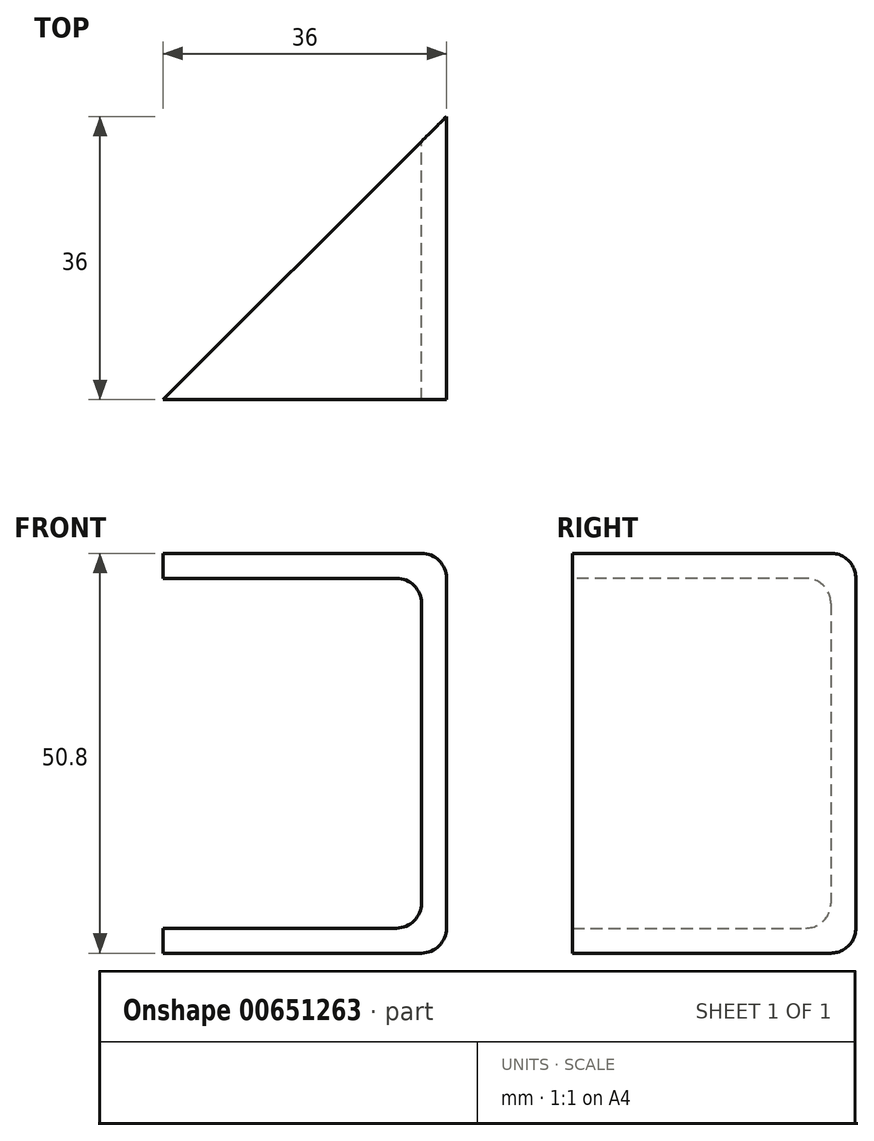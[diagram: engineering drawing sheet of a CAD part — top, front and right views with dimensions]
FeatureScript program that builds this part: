
annotation { "Feature Type Name" : "Feature", "Feature Type Description" : "" }
export const myFeature = defineFeature(function(context is Context, id is Id, definition is map)
    precondition{}
    {
        {
            var Q0;
            Q0=qCreatedBy(makeId("Front.planeOp"),FACE);
            var sketch = newSketch(context, id + "F0", { "sketchPlane" : qUnion([Q0])});
            skLineSegment(sketch, "E0.bottom", {"start": v(-38.1, -22.23) * mm, "end": v(-38.1, 22.22) * mm});
            skLineSegment(sketch, "E0.top", {"start": v(38.1, -22.23) * mm, "end": v(38.1, 22.22) * mm});
            skLineSegment(sketch, "E0.left", {"start": v(-34.92, -25.4) * mm, "end": v(34.93, -25.4) * mm});
            skLineSegment(sketch, "E0.right", {"start": v(-34.93, 25.4) * mm, "end": v(34.92, 25.4) * mm});
            skPoint(sketch, "E0.middle", {"position": v(0, 0) * mm});
            skLineSegment(sketch, "E1.bottom", {"start": v(34.93, 19.05) * mm, "end": v(34.93, -19.05) * mm});
            skLineSegment(sketch, "E1.top", {"start": v(-34.93, 19.05) * mm, "end": v(-34.93, -19.05) * mm});
            skLineSegment(sketch, "E1.left", {"start": v(31.75, 22.23) * mm, "end": v(-31.75, 22.23) * mm});
            skLineSegment(sketch, "E1.right", {"start": v(31.75, -22.22) * mm, "end": v(-31.75, -22.22) * mm});
            skPoint(sketch, "E2.visualSharp", {"position": v(34.93, 22.23) * mm});
            skArc(sketch, "E2.filletArc", {"start": v(34.93, 19.05) * mm, "mid": v(34, 21.3) * mm, "end": v(31.75, 22.23) * mm});
            skPoint(sketch, "E3.visualSharp", {"position": v(34.93, -22.22) * mm});
            skArc(sketch, "E3.filletArc", {"start": v(31.75, -22.22) * mm, "mid": v(34, -21.3) * mm, "end": v(34.93, -19.05) * mm});
            skPoint(sketch, "E4.visualSharp", {"position": v(38.1, -25.4) * mm});
            skPoint(sketch, "E5.visualSharp", {"position": v(-38.1, -25.4) * mm});
            skPoint(sketch, "E6.visualSharp", {"position": v(-34.93, -22.22) * mm});
            skArc(sketch, "E6.filletArc", {"start": v(-34.93, -19.05) * mm, "mid": v(-34, -21.3) * mm, "end": v(-31.75, -22.22) * mm});
            skPoint(sketch, "E7.visualSharp", {"position": v(-38.1, 25.4) * mm});
            skPoint(sketch, "E8.visualSharp", {"position": v(-34.93, 22.23) * mm});
            skArc(sketch, "E8.filletArc", {"start": v(-31.75, 22.23) * mm, "mid": v(-34, 21.3) * mm, "end": v(-34.93, 19.05) * mm});
            skPoint(sketch, "E9.visualSharp", {"position": v(38.1, 25.4) * mm});
            skLineSegment(sketch, "E10", {"start": v(34.92, 25.4) * mm, "end": v(38.1, 25.4) * mm});
            skLineSegment(sketch, "E11", {"start": v(38.1, 22.22) * mm, "end": v(38.1, 25.4) * mm});
            skLineSegment(sketch, "E12", {"start": v(-34.93, 25.4) * mm, "end": v(-38.1, 25.4) * mm});
            skLineSegment(sketch, "E13", {"start": v(-38.1, 22.22) * mm, "end": v(-38.1, 25.4) * mm});
            skLineSegment(sketch, "E14", {"start": v(-38.1, -22.23) * mm, "end": v(-38.1, -25.4) * mm});
            skLineSegment(sketch, "E15", {"start": v(-34.92, -25.4) * mm, "end": v(-38.1, -25.4) * mm});
            skLineSegment(sketch, "E16", {"start": v(34.93, -25.4) * mm, "end": v(38.1, -25.4) * mm});
            skLineSegment(sketch, "E17", {"start": v(38.1, -22.23) * mm, "end": v(38.1, -25.4) * mm});
            skSolve(sketch);
        }
        {
            assignVariable(context, id + "F1", {"name" : "Length", "anyValue" : 36});
        }
        {
            var Q0;
            Q0=makeQuery(id+"F0.imprint","IMPRINT",FACE,{"disambiguationData":[TD([[makeQuery(id+"F0.imprint","IMPRINT",EDGE,{"derivedFrom":sQuery(id+"F0.wireOp",EDGE,"E0.bottom")}),-1.0]])]});
            extrude(context, id + "F2", {"entities" : qUnion([Q0]), "depth" : (getVariable(context, 'Length')) * mm, "offsetDistance" : 25.4 * mm});
        }
        {
            var Q0;
            Q0=makeQuery(id+"F2.opExtrude","SWEPT_FACE",FACE,{"disambiguationData":[OSD([sQuery(id+"F0.wireOp",EDGE,"E0.right"),sQuery(id+"F0.wireOp",EDGE,"E10"),sQuery(id+"F0.wireOp",EDGE,"E12")])]});
            var sketch = newSketch(context, id + "F3", { "sketchPlane" : qUnion([Q0])});
            skLineSegment(sketch, "E18", {"start": v(-38.1, 0) * mm, "end": v(-38.1, -76.2) * mm});
            skLineSegment(sketch, "E19", {"start": v(-38.1, -76.2) * mm, "end": v(38.1, 0) * mm});
            skLineSegment(sketch, "E20", {"start": v(38.1, 0) * mm, "end": v(-38.1, 0) * mm});
            skSolve(sketch);
        }
        {
            var Q0;
            Q0=makeQuery(id+"F3.imprint","IMPRINT",FACE,{"disambiguationData":[TD([[makeQuery(id+"F3.imprint","IMPRINT",EDGE,{"derivedFrom":sQuery(id+"F3.wireOp",EDGE,"E18")}),-1.0]])]});
            extrude(context, id + "F4", {"entities" : qUnion([Q0]), "operationType" : NewBodyOperationType.REMOVE, "endBound" : BoundingType.THROUGH_ALL, "oppositeDirection" : true, "depth" : 25.4 * mm, "offsetDistance" : 25.4 * mm});
        }
        {
            var Q0;
            Q0=makeQuery(id+"F2.opExtrude","SWEPT_FACE",FACE,{"disambiguationData":[OSD([sQuery(id+"F0.wireOp",EDGE,"E0.right"),sQuery(id+"F0.wireOp",EDGE,"E10"),sQuery(id+"F0.wireOp",EDGE,"E12")])]});
            var sketch = newSketch(context, id + "F5", { "sketchPlane" : qUnion([Q0])});
            skLineSegment(sketch, "E21", {"start": v(38.1, -914.4) * mm, "end": v(-38.1, -838.2) * mm});
            skLineSegment(sketch, "E22", {"start": v(-38.1, -838.2) * mm, "end": v(-38.1, -914.4) * mm});
            skLineSegment(sketch, "E23", {"start": v(-38.1, -914.4) * mm, "end": v(38.1, -914.4) * mm});
            skSolve(sketch);
        }
        {
            var Q0;
            Q0=makeQuery(id+"F5.imprint","IMPRINT",FACE,{"disambiguationData":[TD([[makeQuery(id+"F5.imprint","IMPRINT",EDGE,{"derivedFrom":sQuery(id+"F5.wireOp",EDGE,"E21")}),1.0]])]});
            extrude(context, id + "F6", {"entities" : qUnion([Q0]), "operationType" : NewBodyOperationType.REMOVE, "endBound" : BoundingType.THROUGH_ALL, "oppositeDirection" : true, "depth" : 25.4 * mm, "offsetDistance" : 25.4 * mm});
        }
        {
            var Q0;
            Q0=makeQuery(id+"F2.opExtrude","SWEPT_EDGE",EDGE,{"disambiguationData":[OSD([sQuery(id+"F0.wireOp",EDGE,"E12"),sQuery(id+"F0.wireOp",EDGE,"E13")])]});
            var Q1;
            Q1=makeQuery(id+"F2.opExtrude","SWEPT_EDGE",EDGE,{"disambiguationData":[OSD([sQuery(id+"F0.wireOp",EDGE,"E14"),sQuery(id+"F0.wireOp",EDGE,"E15")])]});
            var Q2;
            Q2=makeQuery(id+"F2.opExtrude","SWEPT_EDGE",EDGE,{"disambiguationData":[OSD([sQuery(id+"F0.wireOp",EDGE,"E10"),sQuery(id+"F0.wireOp",EDGE,"E11")])]});
            var Q3;
            Q3=makeQuery(id+"F2.opExtrude","SWEPT_EDGE",EDGE,{"disambiguationData":[OSD([sQuery(id+"F0.wireOp",EDGE,"E16"),sQuery(id+"F0.wireOp",EDGE,"E17")])]});
            fillet(context, id + "F7", {"entities" : qUnion([Q0, Q1, Q2, Q3]), "radius" : 3.17 * mm, "tangentPropagation" : true, "allowEdgeOverflow" : false});
        }
    });
